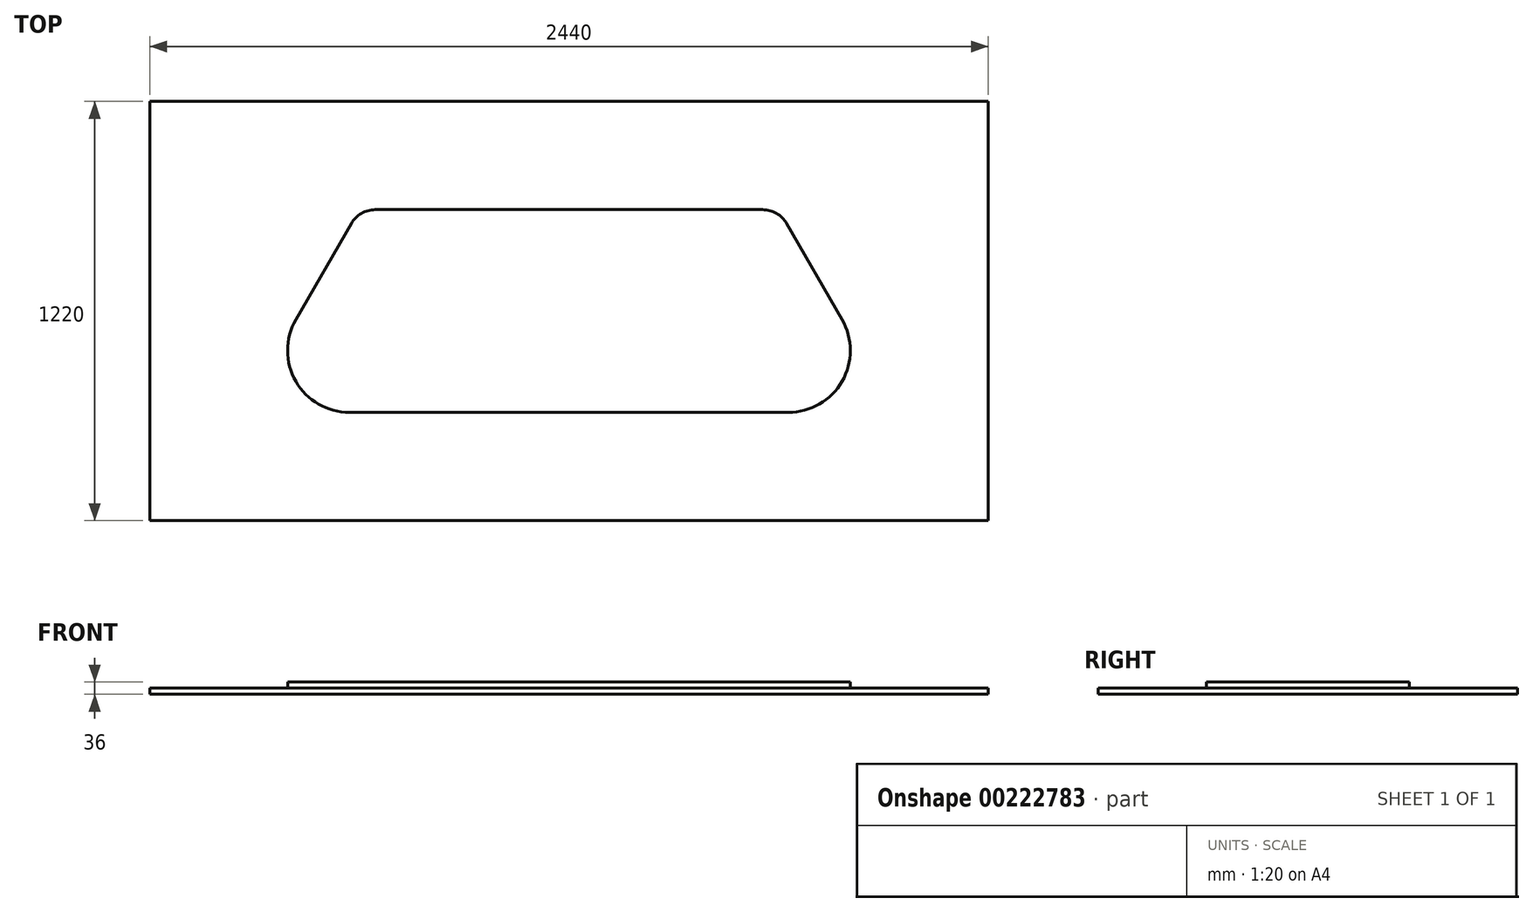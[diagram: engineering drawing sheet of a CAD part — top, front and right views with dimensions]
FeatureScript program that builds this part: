
annotation { "Feature Type Name" : "Feature", "Feature Type Description" : "" }
export const myFeature = defineFeature(function(context is Context, id is Id, definition is map)
    precondition{}
    {
        {
            var Q0;
            Q0=qCreatedBy(makeId("Top.planeOp"),FACE);
            var sketch = newSketch(context, id + "F0", { "sketchPlane" : qUnion([Q0])});
            skLineSegment(sketch, "E0.bottom", {"start": v(-590, 290) * mm, "end": v(590, 290) * mm, "construction": true});
            skLineSegment(sketch, "E0.top", {"start": v(-590, -290) * mm, "end": v(590, -290) * mm, "construction": true});
            skLineSegment(sketch, "E0.left", {"start": v(-590, 290) * mm, "end": v(-590, -290) * mm, "construction": true});
            skLineSegment(sketch, "E0.right", {"start": v(590, 290) * mm, "end": v(590, -290) * mm, "construction": true});
            skPoint(sketch, "E0.middle", {"position": v(0, 0) * mm});
            skLineSegment(sketch, "E1", {"start": v(0, 254.16) * mm, "end": v(0, -247.53) * mm, "construction": true});
            skLineSegment(sketch, "E2", {"start": v(-547.35, 0) * mm, "end": v(503.45, 0) * mm, "construction": true});
            skLineSegment(sketch, "E3.0", {"start": v(-610, 295) * mm, "end": v(610, 295) * mm});
            skLineSegment(sketch, "E3.2", {"start": v(-950.64, -295) * mm, "end": v(950.64, -295) * mm});
            skLineSegment(sketch, "E4", {"start": v(-610, 295) * mm, "end": v(-950.64, -295) * mm});
            skLineSegment(sketch, "E5.MirrorCS", {"start": v(610, 295) * mm, "end": v(950.64, -295) * mm});
            skSolve(sketch);
        }
        {
            var Q0;
            Q0=qSketchRegion(id+"F0",true);
            extrude(context, id + "F1", {"entities" : qUnion([Q0]), "depth" : 18 * mm});
        }
        {
            var Q0;
            Q0=qCreatedBy(makeId("Top.planeOp"),FACE);
            var sketch = newSketch(context, id + "F2", { "sketchPlane" : qUnion([Q0])});
            skLineSegment(sketch, "E6.bottom", {"start": v(-1220, 610) * mm, "end": v(1220, 610) * mm});
            skLineSegment(sketch, "E6.top", {"start": v(-1220, -610) * mm, "end": v(1220, -610) * mm});
            skLineSegment(sketch, "E6.left", {"start": v(-1220, 610) * mm, "end": v(-1220, -610) * mm});
            skLineSegment(sketch, "E6.right", {"start": v(1220, 610) * mm, "end": v(1220, -610) * mm});
            skPoint(sketch, "E6.middle", {"position": v(0, 0) * mm});
            skSolve(sketch);
        }
        {
            var Q0;
            Q0=qSketchRegion(id+"F2",true);
            extrude(context, id + "F3", {"entities" : qUnion([Q0]), "oppositeDirection" : true, "depth" : 18 * mm});
        }
        {
            var Q0;
            Q0=makeQuery(id+"F1.opExtrude","SWEPT_EDGE",EDGE,{"disambiguationData":[OSD([sQuery(id+"F0.wireOp",EDGE,"E3.2"),sQuery(id+"F0.wireOp",EDGE,"E4")])]});
            var Q1;
            Q1=makeQuery(id+"F1.opExtrude","SWEPT_EDGE",EDGE,{"disambiguationData":[OSD([sQuery(id+"F0.wireOp",EDGE,"E3.2"),sQuery(id+"F0.wireOp",EDGE,"E5.MirrorCS")])]});
            fillet(context, id + "F4", {"entities" : qUnion([Q0, Q1]), "radius" : 180 * mm, "tangentPropagation" : true, "allowEdgeOverflow" : false});
        }
        {
            var Q0;
            Q0=makeQuery(id+"F1.opExtrude","SWEPT_EDGE",EDGE,{"disambiguationData":[OSD([sQuery(id+"F0.wireOp",EDGE,"E3.0"),sQuery(id+"F0.wireOp",EDGE,"E4")])]});
            var Q1;
            Q1=makeQuery(id+"F1.opExtrude","SWEPT_EDGE",EDGE,{"disambiguationData":[OSD([sQuery(id+"F0.wireOp",EDGE,"E3.0"),sQuery(id+"F0.wireOp",EDGE,"E5.MirrorCS")])]});
            fillet(context, id + "F5", {"entities" : qUnion([Q0, Q1]), "radius" : 80 * mm, "tangentPropagation" : true, "allowEdgeOverflow" : false});
        }
    });
